# Revit family: Shower-Valve_Trim-KOHLER-Aleo-K-77310IN
name_source: partatom
category: Specialty Equipment
revit_build: Autodesk Revit 2017 (Build: 20160225_1515(x64)
units: mm (PartAtom-declared; Revit-internal decimal feet)

## family parameters
Cut with Voids When Loaded = No
Host = Face
OmniClass Number = 23.31.25.00
OmniClass Title = Toilet and Bath Specialties
Part Type = Normal
Room Calculation Point = No
Round Connector Dimension = Use Diameter
Shared = No

## types (3) — shared parameters
ADA Compliant = No
Assembly Code = C1030200
Date Modified = 10/20/2020
Default Elevation = 42"
Description = Aqua turbo 360 trim
Height = 8 1/4"
Length = 3"
Manufacturer = KOHLER Co.
Master Format 2014 = 10 28 00
Master Format 2014 Name = Toilet, Bath, and Laundry Accessories
Material = Premium Metal Construction
Product Name = Aleo
Product Page URL = https://www.kohler.co.in
URL = https://www.kohler.co.in
WaterSense Certified = No
Width = 5 1/2"

## per-type parameters (varying)
| type | Finish | Model | Type |
| CP- Polished Chrome | Kohler-Metal-CP-Polished_Chrome | K-77310IN-4FP-CP | 1 |
| BV- Brushed Bronze | Kohler-Metal-BV-Brushed_Bronze | K-77310IN-4FP-BV | 2 |
| RGD- Rose Gold | Kohler-Metal-RGD-Polished_Rose_Gold | K-77310IN-4FP-RGD | 3 |

## geometry (parser evidence)
native form markers: Sweep x10
no freeform markers — native parametric forms only
